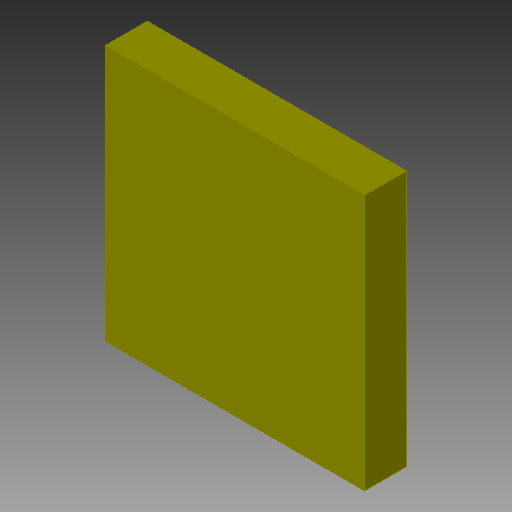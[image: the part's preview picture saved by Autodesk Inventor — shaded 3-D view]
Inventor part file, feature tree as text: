
AUTODESK INVENTOR PART (.ipt)
format: ipt  version: 2018 (Build 220112000, 112)  size: 80,896 bytes
history: native  units: in
note: dims shown in document units (in); Inventor stores cm internally (conversion verified against a paired STEP export)
features: other x1, extrude x1
ambient origin geometry x8: Origin, YZ Plane, XZ Plane, XY Plane, X Axis, Y Axis, Z Axis, Center Point
bodies: Solid1 (feature_tree)
feature tree (2):
  other  "PBTH, S1_PBTH_138"
  extrude  "Extrusion1"  Depth=0.0394in TaperAngle=0.0deg
